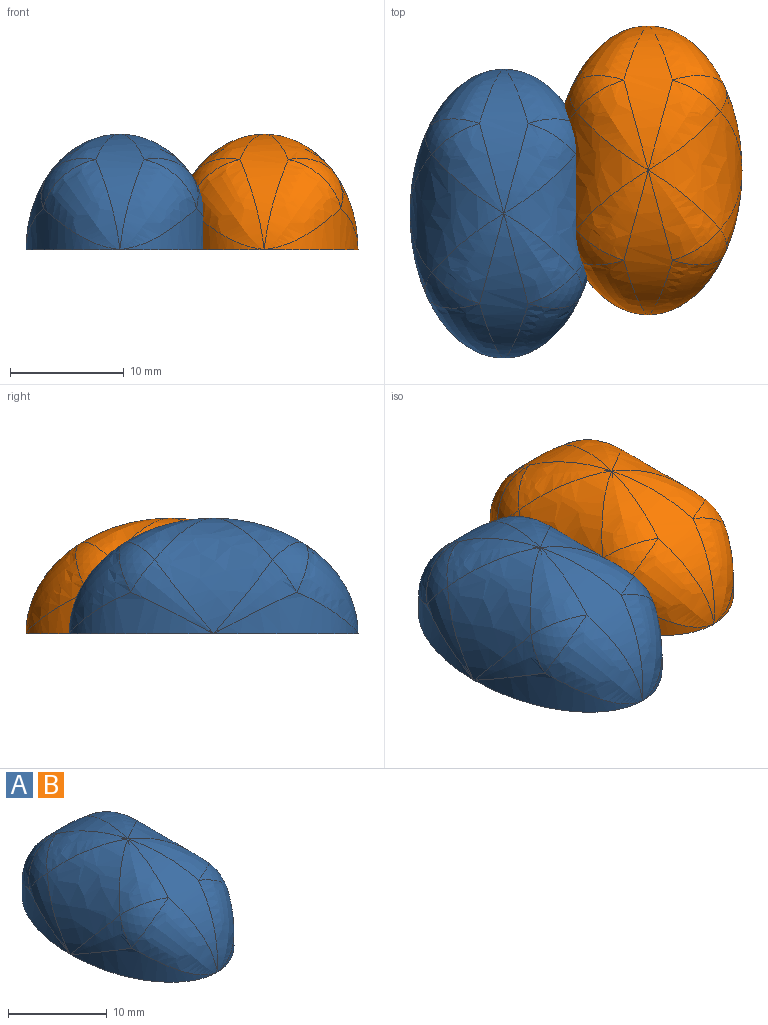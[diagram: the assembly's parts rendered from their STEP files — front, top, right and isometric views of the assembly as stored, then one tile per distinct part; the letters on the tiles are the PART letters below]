
ASSEMBLY  parts=2 mates=1
PART A: 25 faces, bbox 16.5x25.4x10.2 mm
  f0: extruded ~12.7x8.26mm, area 31.2mm2, adj f6,f17,f20
  f1: extruded ~12.7x8.26mm, area 31.2mm2, adj f6,f14,f16
  f2: extruded ~12.7x8.25mm, area 31.2mm2, adj f6,f9,f12
  f3: extruded ~12.7x8.26mm, area 31.2mm2, adj f6,f22,f24
  f4: extruded ~10.38x10.16mm, area 75.8mm2, adj f9,f10,f13,f14
  f5: extruded ~10.38x10.16mm, area 75.8mm2, adj f17,f18,f21,f22
  f6: plane 25.41x16.52mm, normal (0,0,-1), area 329.4mm2, adj f0,f1,f2,f3
  f7: extruded ~12.7x10.16mm, area 38.8mm2, adj f13,f16,f18,f20
  f8: extruded ~12.7x10.16mm, area 38.8mm2, adj f10,f12,f21,f24
  f9: bspline ~7.69x6.85mm, area 9.9mm2, adj f2,f4,f11
  f10: bspline ~8.54x6.66mm, area 17mm2, adj f4,f8,f11
  f11: sphere r=5.08mm, area 12.1mm2, adj f9,f10,f12
  f12: bspline ~8.23x6.95mm, area 41mm2, adj f2,f8,f11
  f13: bspline ~8.54x6.66mm, area 17mm2, adj f4,f7,f15
  f14: bspline ~7.69x6.85mm, area 14.4mm2, adj f1,f4,f15
  f15: sphere r=5.08mm, area 12.1mm2, adj f13,f14,f16
  f16: bspline ~8.23x6.95mm, area 41mm2, adj f1,f7,f15
  f17: bspline ~7.5x6.68mm, area 9.9mm2, adj f0,f5,f19
  f18: bspline ~8.54x6.66mm, area 17mm2, adj f5,f7,f19
  f19: sphere r=5.08mm, area 11.8mm2, adj f17,f18,f20
  f20: bspline ~8.23x6.95mm, area 41mm2, adj f0,f7,f19
  f21: bspline ~8.54x6.66mm, area 17mm2, adj f5,f8,f23
  f22: bspline ~7.5x6.68mm, area 14.4mm2, adj f3,f5,f23
  f23: sphere r=5.08mm, area 11.8mm2, adj f21,f22,f24
  f24: bspline ~8.23x6.95mm, area 41mm2, adj f3,f8,f23
PART B: same geometry as A
PLACE A t=(13.41,9.01,-3.18)mm
PLACE B t=(26.11,12.82,-3.18)mm
MATE fastened B.f6 <-> A.f6  axis (0,0,-1) through (26.11,12.82,-3.18)mm
